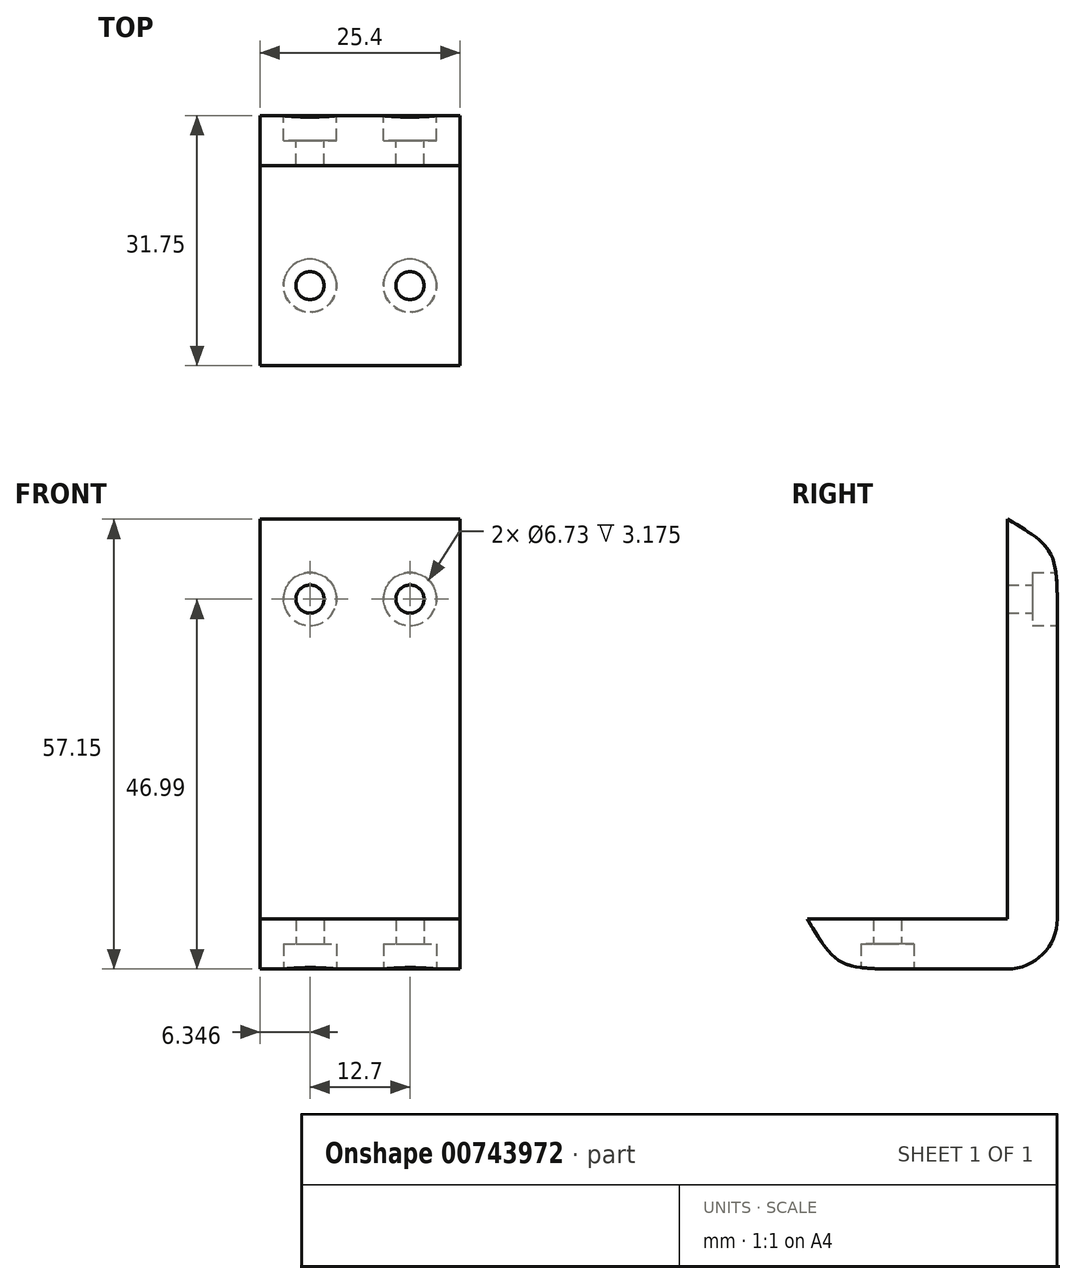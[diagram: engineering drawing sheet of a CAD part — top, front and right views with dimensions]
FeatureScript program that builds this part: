
annotation { "Feature Type Name" : "Feature", "Feature Type Description" : "" }
export const myFeature = defineFeature(function(context is Context, id is Id, definition is map)
    precondition{}
    {
        {
            var Q0;
            Q0=qCreatedBy(makeId("Top.planeOp"),FACE);
            var sketch = newSketch(context, id + "F0", { "sketchPlane" : qUnion([Q0])});
            skLineSegment(sketch, "E0.bottom", {"start": v(-22.3, -31.75) * mm, "end": v(3.1, -31.75) * mm});
            skLineSegment(sketch, "E0.top", {"start": v(-22.3, 0) * mm, "end": v(3.1, 0) * mm});
            skLineSegment(sketch, "E0.left", {"start": v(-22.3, -31.75) * mm, "end": v(-22.3, 0) * mm});
            skLineSegment(sketch, "E0.right", {"start": v(3.1, -31.75) * mm, "end": v(3.1, 0) * mm});
            skSolve(sketch);
        }
        {
            var Q0;
            Q0 = qSketchRegion(id + "F0", true);
            extrude(context, id + "F1", {"entities" : qUnion([Q0]), "depth" : 6.35 * mm, "offsetDistance" : 25.4 * mm});
        }
        {
            var Q0;
            Q0=makeQuery(id+"F1.opExtrude","CAP_FACE",FACE,{"disambiguationData":[OSD([sQuery(id+"F0.wireOp",EDGE,"E0.bottom"),sQuery(id+"F0.wireOp",EDGE,"E0.top"),sQuery(id+"F0.wireOp",EDGE,"E0.left"),sQuery(id+"F0.wireOp",EDGE,"E0.right")])],"isStart":false});
            var sketch = newSketch(context, id + "F2", { "sketchPlane" : qUnion([Q0])});
            skLineSegment(sketch, "E1.bottom", {"start": v(-22.3, 0) * mm, "end": v(3.1, 0) * mm});
            skLineSegment(sketch, "E1.top", {"start": v(-22.3, -6.35) * mm, "end": v(3.1, -6.35) * mm});
            skLineSegment(sketch, "E1.left", {"start": v(-22.3, 0) * mm, "end": v(-22.3, -6.35) * mm});
            skLineSegment(sketch, "E1.right", {"start": v(3.1, 0) * mm, "end": v(3.1, -6.35) * mm});
            skSolve(sketch);
        }
        {
            var Q0;
            Q0 = qSketchRegion(id + "F2", true);
            extrude(context, id + "F3", {"entities" : qUnion([Q0]), "operationType" : NewBodyOperationType.ADD, "depth" : 50.8 * mm, "offsetDistance" : 25.4 * mm});
        }
        {
            var Q0;
            Q0=makeQuery(id+"F1.opExtrude","CAP_EDGE",EDGE,{"disambiguationData":[OSD([sQuery(id+"F0.wireOp",EDGE,"E0.top")])],"isStart":true});
            fillet(context, id + "F4", {"entities" : qUnion([Q0]), "radius" : 6.35 * mm, "tangentPropagation" : true, "allowEdgeOverflow" : false});
        }
        {
            var Q0;
            Q0=makeQuery(id+"F1.opExtrude","CAP_FACE",FACE,{"disambiguationData":[OSD([sQuery(id+"F0.wireOp",EDGE,"E0.bottom"),sQuery(id+"F0.wireOp",EDGE,"E0.top"),sQuery(id+"F0.wireOp",EDGE,"E0.left"),sQuery(id+"F0.wireOp",EDGE,"E0.right")])],"isStart":true});
            var sketch = newSketch(context, id + "F5", { "sketchPlane" : qUnion([Q0])});
            skLineSegment(sketch, "E2", {"start": v(-9.6, 31.75) * mm, "end": v(-9.6, 21.59) * mm, "construction": true});
            skLineSegment(sketch, "E3", {"start": v(-9.6, 21.59) * mm, "end": v(-3.24, 21.59) * mm, "construction": true});
            skLineSegment(sketch, "E4", {"start": v(-9.6, 21.59) * mm, "end": v(-15.94, 21.59) * mm, "construction": true});
            skCircle(sketch, "E5", {"center": v(-15.94, 21.59) * mm, "radius": 3.37 * mm});
            skCircle(sketch, "E6", {"center": v(-3.24, 21.59) * mm, "radius": 3.37 * mm});
            skSolve(sketch);
        }
        {
            var Q0;
            Q0 = qSketchRegion(id + "F5", true);
            extrude(context, id + "F6", {"entities" : qUnion([Q0]), "operationType" : NewBodyOperationType.REMOVE, "oppositeDirection" : true, "depth" : 3.17 * mm, "offsetDistance" : 25.4 * mm});
        }
        {
            var Q0;
            Q0=makeQuery(id+"F6.boolean.opBoolean","COPY",FACE,{"derivedFrom":makeQuery(id+"F6.opExtrude","CAP_FACE",FACE,{"disambiguationData":[OSD([sQuery(id+"F5.wireOp",EDGE,"E6")])],"isStart":false})});
            var sketch = newSketch(context, id + "F7", { "sketchPlane" : qUnion([Q0])});
            skCircle(sketch, "E7", {"center": v(-3.24, 21.59) * mm, "radius": 1.78 * mm});
            skSolve(sketch);
        }
        {
            var Q0;
            Q0 = qSketchRegion(id + "F7", true);
            extrude(context, id + "F8", {"entities" : qUnion([Q0]), "operationType" : NewBodyOperationType.REMOVE, "oppositeDirection" : true, "depth" : 25.4 * mm, "offsetDistance" : 25.4 * mm});
        }
        {
            var Q0;
            Q0=makeQuery(id+"F6.boolean.opBoolean","COPY",FACE,{"derivedFrom":makeQuery(id+"F6.opExtrude","CAP_FACE",FACE,{"disambiguationData":[OSD([sQuery(id+"F5.wireOp",EDGE,"E5")])],"isStart":false})});
            var sketch = newSketch(context, id + "F9", { "sketchPlane" : qUnion([Q0])});
            skCircle(sketch, "E8", {"center": v(-15.94, 21.59) * mm, "radius": 1.78 * mm});
            skSolve(sketch);
        }
        {
            var Q0;
            Q0 = qSketchRegion(id + "F9", true);
            extrude(context, id + "F10", {"entities" : qUnion([Q0]), "operationType" : NewBodyOperationType.REMOVE, "oppositeDirection" : true, "depth" : 25.4 * mm, "offsetDistance" : 25.4 * mm});
        }
        {
            var Q0;
            Q0=makeQuery(id+"F3.boolean.opBoolean","MERGE",FACE,{"derivedFrom":[makeQuery(id+"F1.opExtrude","SWEPT_FACE",FACE,{"disambiguationData":[OSD([sQuery(id+"F0.wireOp",EDGE,"E0.top")])]}),makeQuery(id+"F3.opExtrude","SWEPT_FACE",FACE,{"disambiguationData":[OSD([sQuery(id+"F2.wireOp",EDGE,"E1.bottom")])]})]});
            var sketch = newSketch(context, id + "F11", { "sketchPlane" : qUnion([Q0])});
            skLineSegment(sketch, "E9", {"start": v(9.6, 57.15) * mm, "end": v(9.6, 47) * mm, "construction": true});
            skLineSegment(sketch, "E10", {"start": v(9.6, 47) * mm, "end": v(15.94, 47) * mm, "construction": true});
            skLineSegment(sketch, "E11", {"start": v(9.6, 47) * mm, "end": v(3.24, 47) * mm, "construction": true});
            skCircle(sketch, "E12", {"center": v(3.24, 47) * mm, "radius": 3.37 * mm});
            skCircle(sketch, "E13", {"center": v(15.94, 47) * mm, "radius": 3.37 * mm});
            skSolve(sketch);
        }
        {
            var Q0;
            Q0=makeQuery(id+"F11.imprint","IMPRINT",FACE,{"disambiguationData":[TD([[makeQuery(id+"F11.imprint","IMPRINT",EDGE,{"derivedFrom":sQuery(id+"F11.wireOp",EDGE,"E12")}),1.0]])]});
            var Q1;
            Q1=makeQuery(id+"F11.imprint","IMPRINT",FACE,{"disambiguationData":[TD([[makeQuery(id+"F11.imprint","IMPRINT",EDGE,{"derivedFrom":sQuery(id+"F11.wireOp",EDGE,"E13")}),1.0]])]});
            extrude(context, id + "F12", {"entities" : qUnion([Q0, Q1]), "operationType" : NewBodyOperationType.REMOVE, "oppositeDirection" : true, "depth" : 3.17 * mm, "offsetDistance" : 25.4 * mm});
        }
        {
            var Q0;
            Q0=makeQuery(id+"F12.boolean.opBoolean","COPY",FACE,{"derivedFrom":makeQuery(id+"F12.opExtrude","CAP_FACE",FACE,{"disambiguationData":[OSD([sQuery(id+"F11.wireOp",EDGE,"E12")])],"isStart":false})});
            var sketch = newSketch(context, id + "F13", { "sketchPlane" : qUnion([Q0])});
            skCircle(sketch, "E14", {"center": v(3.24, 47) * mm, "radius": 1.78 * mm});
            skSolve(sketch);
        }
        {
            var Q0;
            Q0 = qSketchRegion(id + "F13", true);
            extrude(context, id + "F14", {"entities" : qUnion([Q0]), "operationType" : NewBodyOperationType.REMOVE, "oppositeDirection" : true, "depth" : 25.4 * mm, "offsetDistance" : 25.4 * mm});
        }
        {
            var Q0;
            Q0=makeQuery(id+"F12.boolean.opBoolean","COPY",FACE,{"derivedFrom":makeQuery(id+"F12.opExtrude","CAP_FACE",FACE,{"disambiguationData":[OSD([sQuery(id+"F11.wireOp",EDGE,"E13")])],"isStart":false})});
            var sketch = newSketch(context, id + "F15", { "sketchPlane" : qUnion([Q0])});
            skCircle(sketch, "E15", {"center": v(15.94, 47) * mm, "radius": 1.78 * mm});
            skSolve(sketch);
        }
        {
            var Q0;
            Q0 = qSketchRegion(id + "F15", true);
            extrude(context, id + "F16", {"entities" : qUnion([Q0]), "operationType" : NewBodyOperationType.REMOVE, "oppositeDirection" : true, "depth" : 25.4 * mm, "offsetDistance" : 25.4 * mm});
        }
        {
            var Q0;
            Q0=makeQuery(id+"F3.opExtrude","CAP_EDGE",EDGE,{"disambiguationData":[OSD([sQuery(id+"F2.wireOp",EDGE,"E1.bottom")])],"isStart":false});
            fillet(context, id + "F17", {"entities" : qUnion([Q0]), "radius" : 12.7 * mm, "tangentPropagation" : true, "rho" : 0.7, "crossSection" : FilletCrossSection.CONIC, "allowEdgeOverflow" : false});
        }
        {
            var Q0;
            Q0=makeQuery(id+"F1.opExtrude","CAP_EDGE",EDGE,{"disambiguationData":[OSD([sQuery(id+"F0.wireOp",EDGE,"E0.bottom")])],"isStart":true});
            fillet(context, id + "F18", {"entities" : qUnion([Q0]), "radius" : 12.7 * mm, "tangentPropagation" : true, "rho" : 0.7, "crossSection" : FilletCrossSection.CONIC, "allowEdgeOverflow" : false});
        }
    });
